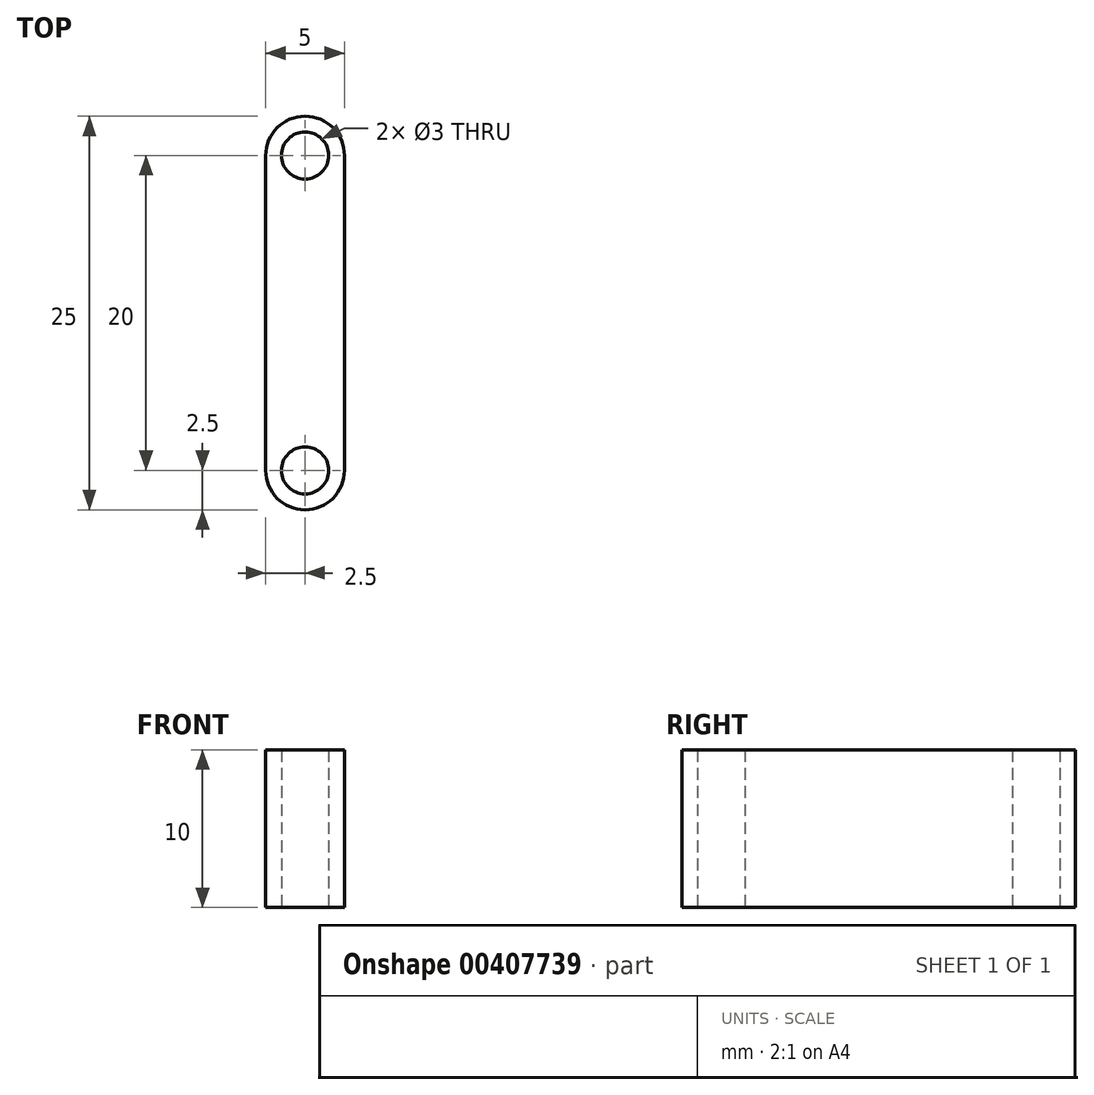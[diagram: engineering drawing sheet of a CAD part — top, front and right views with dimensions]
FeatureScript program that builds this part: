
annotation { "Feature Type Name" : "Feature", "Feature Type Description" : "" }
export const myFeature = defineFeature(function(context is Context, id is Id, definition is map)
    precondition{}
    {
        {
            var Q0;
            Q0=qCreatedBy(makeId("Top.planeOp"),FACE);
            var sketch = newSketch(context, id + "F0", { "sketchPlane" : qUnion([Q0])});
            skCircle(sketch, "E0", {"center": v(0, 10) * mm, "radius": 1.5 * mm});
            skCircle(sketch, "E1", {"center": v(0, -10) * mm, "radius": 1.5 * mm});
            skLineSegment(sketch, "E2", {"start": v(-2.5, 10) * mm, "end": v(-2.5, -10) * mm});
            skLineSegment(sketch, "E3", {"start": v(2.5, -10) * mm, "end": v(2.5, 10) * mm});
            skArc(sketch, "E4", {"start": v(-2.5, 10) * mm, "mid": v(0, 12.5) * mm, "end": v(2.5, 10) * mm});
            skArc(sketch, "E5", {"start": v(2.5, -10) * mm, "mid": v(0, -12.5) * mm, "end": v(-2.5, -10) * mm});
            skSolve(sketch);
        }
        {
            var Q0;
            Q0 = qSketchRegion(id + "F0", true);
            extrude(context, id + "F1", {"entities" : qUnion([Q0]), "depth" : 10 * mm, "symmetric" : true});
        }
    });
